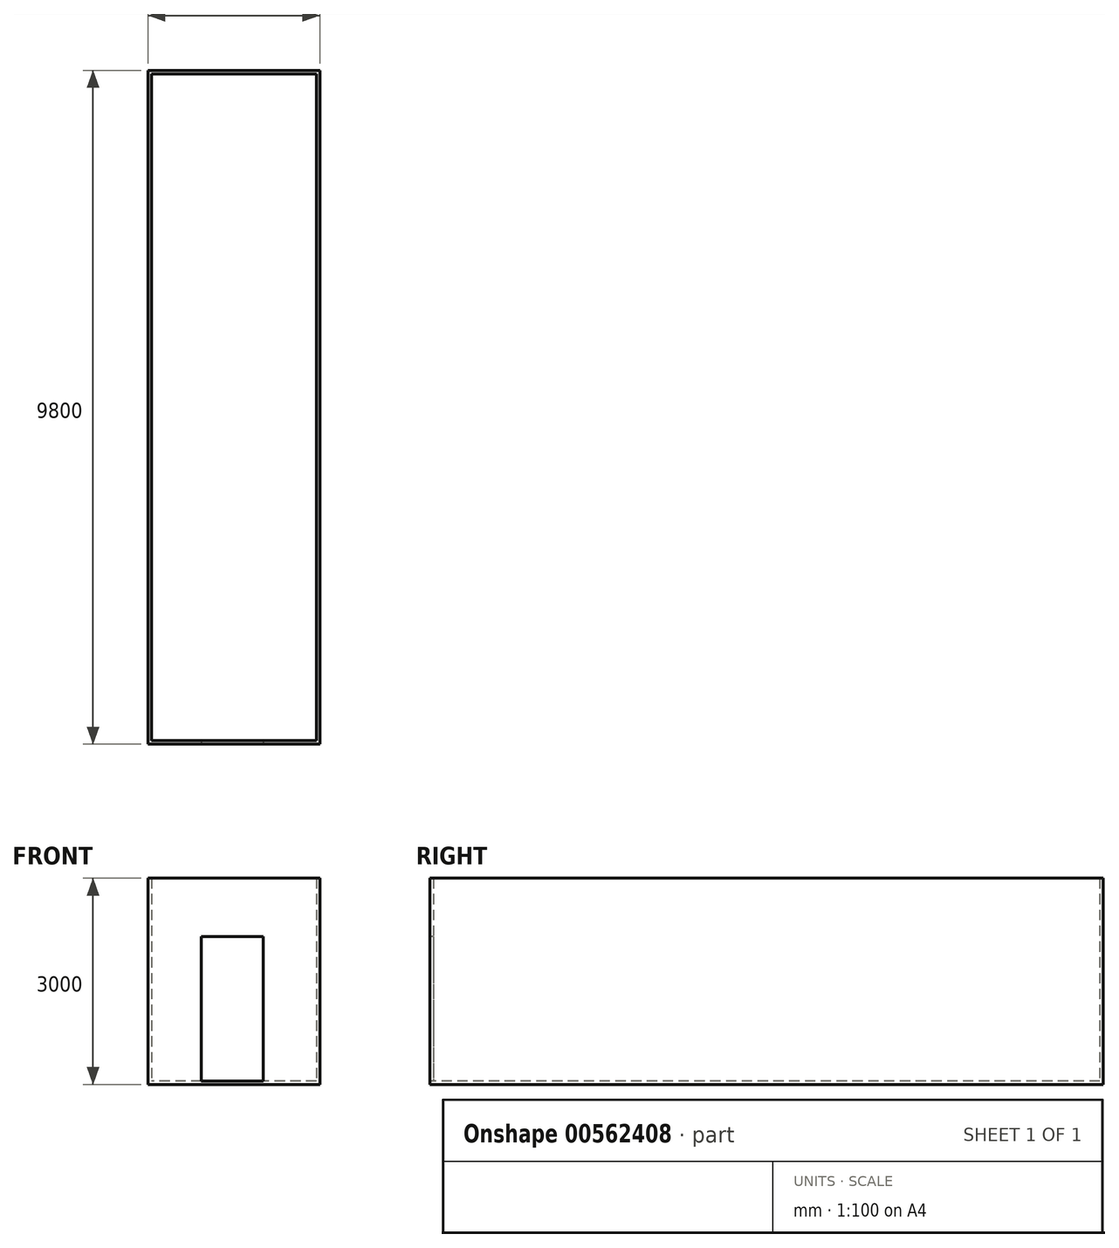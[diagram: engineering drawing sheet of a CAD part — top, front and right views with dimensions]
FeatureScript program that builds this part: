
annotation { "Feature Type Name" : "Feature", "Feature Type Description" : "" }
export const myFeature = defineFeature(function(context is Context, id is Id, definition is map)
    precondition{}
    {
        {
            var Q0;
            Q0=qCreatedBy(makeId("Top.planeOp"),FACE);
            var sketch = newSketch(context, id + "F0", { "sketchPlane" : qUnion([Q0])});
            skLineSegment(sketch, "E0.bottom", {"start": v(1250, 4900) * mm, "end": v(-1250, 4900) * mm});
            skLineSegment(sketch, "E0.top", {"start": v(1250, -4900) * mm, "end": v(-1250, -4900) * mm});
            skLineSegment(sketch, "E0.left", {"start": v(1250, 4900) * mm, "end": v(1250, -4900) * mm});
            skLineSegment(sketch, "E0.right", {"start": v(-1250, 4900) * mm, "end": v(-1250, -4900) * mm});
            skPoint(sketch, "E0.middle", {"position": v(0, 0) * mm});
            skSolve(sketch);
        }
        {
            var Q0;
            Q0 = qSketchRegion(id + "F0", true);
            extrude(context, id + "F1", {"entities" : qUnion([Q0]), "depth" : 3000 * mm, "offsetDistance" : 25 * mm});
        }
        {
            var Q0;
            Q0=makeQuery(id+"F1.opExtrude","CAP_FACE",FACE,{"disambiguationData":[OSD([sQuery(id+"F0.wireOp",EDGE,"E0.bottom"),sQuery(id+"F0.wireOp",EDGE,"E0.top"),sQuery(id+"F0.wireOp",EDGE,"E0.left"),sQuery(id+"F0.wireOp",EDGE,"E0.right")])],"isStart":false});
            shell(context, id + "F2", {"entities" : qUnion([Q0]), "thickness" : 50 * mm});
        }
        {
            var Q0;
            Q0=makeQuery(id+"F1.opExtrude","SWEPT_FACE",FACE,{"disambiguationData":[OSD([sQuery(id+"F0.wireOp",EDGE,"E0.top")])]});
            var sketch = newSketch(context, id + "F3", { "sketchPlane" : qUnion([Q0])});
            skLineSegment(sketch, "E1", {"start": v(-473.53, 50) * mm, "end": v(426.47, 50) * mm});
            skLineSegment(sketch, "E2", {"start": v(426.47, 50) * mm, "end": v(426.47, 2150) * mm});
            skLineSegment(sketch, "E3", {"start": v(426.47, 2150) * mm, "end": v(-473.53, 2150) * mm});
            skLineSegment(sketch, "E4", {"start": v(-473.53, 2150) * mm, "end": v(-473.53, 50) * mm});
            skSolve(sketch);
        }
        {
            var Q0;
            Q0 = qSketchRegion(id + "F3", true);
            extrude(context, id + "F4", {"entities" : qUnion([Q0]), "operationType" : NewBodyOperationType.REMOVE, "oppositeDirection" : true, "depth" : 50 * mm, "offsetDistance" : 25 * mm});
        }
    });
